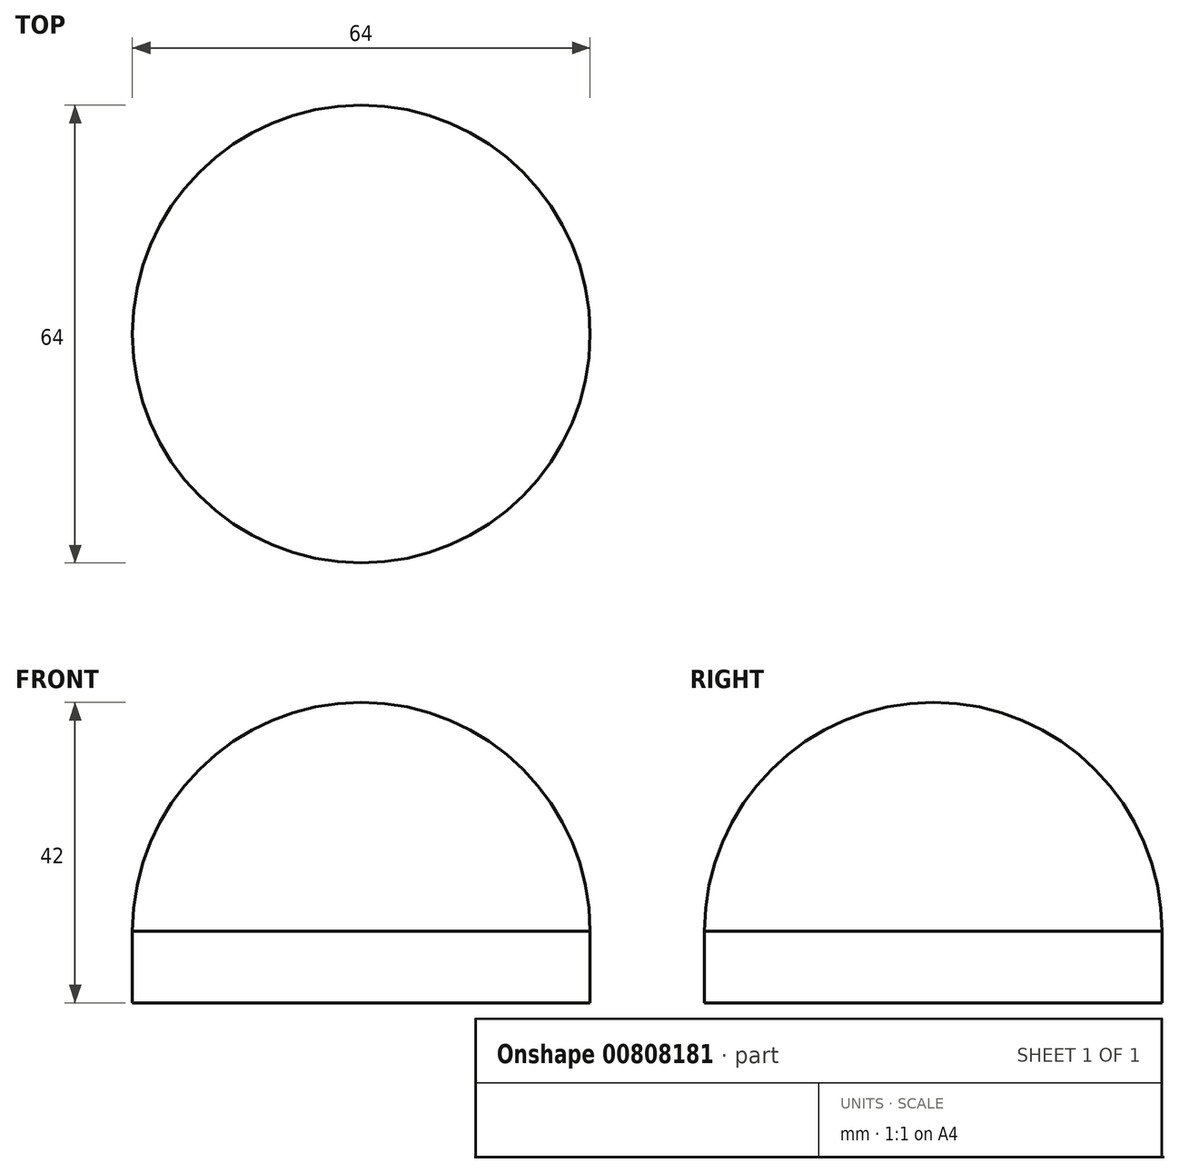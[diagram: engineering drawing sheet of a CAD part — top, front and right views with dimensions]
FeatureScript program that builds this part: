
annotation { "Feature Type Name" : "Feature", "Feature Type Description" : "" }
export const myFeature = defineFeature(function(context is Context, id is Id, definition is map)
    precondition{}
    {
        {
            var Q0;
            Q0=qCreatedBy(makeId("Top.planeOp"),FACE);
            var sketch = newSketch(context, id + "F0", { "sketchPlane" : qUnion([Q0])});
            skCircle(sketch, "E0", {"center": v(0, 0) * mm, "radius": 32 * mm});
            skLineSegment(sketch, "E1", {"start": v(0, 32) * mm, "end": v(0, -32) * mm});
            skSolve(sketch);
        }
        {
            var Q0;
            Q0=makeQuery(id+"F0.imprint","IMPRINT",FACE,{"disambiguationData":[TD([[makeQuery(id+"F0.imprint","IMPRINT",EDGE,{"derivedFrom":sQuery(id+"F0.wireOp",EDGE,"E0")}),1.0]])]});
            extrude(context, id + "F1", {"entities" : qUnion([Q0]), "oppositeDirection" : true, "depth" : 10 * mm, "offsetDistance" : 25 * mm});
        }
        {
            var Q0;
            {var subQ0=sQuery(id+"F0.wireOp",EDGE,"E1");Q0=makeQuery(id+"F0.imprint","IMPRINT",FACE,{"disambiguationData":[TD([[makeQuery(id+"F0.imprint","IMPRINT",EDGE,{"derivedFrom":subQ0}),-1.0]])]});}
            var Q1;
            Q1=sQuery(id+"F0.wireOp",EDGE,"E1");
            revolve(context, id + "F2", {"surfaceOperationType" : NewSurfaceOperationType.NEW, "entities" : qUnion([Q0]), "axis" : qUnion([Q1]), "revolveType" : RevolveType.ONE_DIRECTION, "oppositeDirection" : true, "angle" : 180 * degree});
        }
    });
